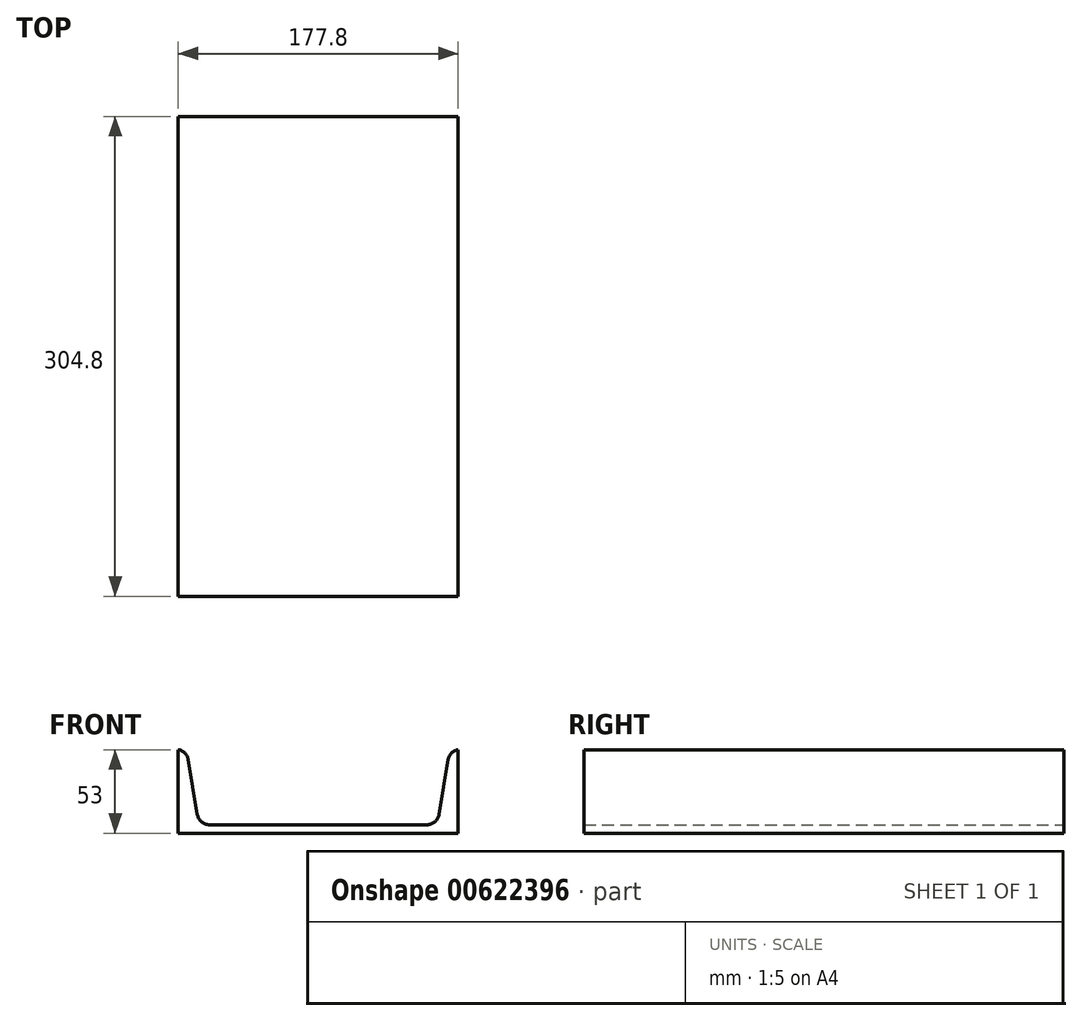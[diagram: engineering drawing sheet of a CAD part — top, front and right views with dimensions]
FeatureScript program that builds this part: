
annotation { "Feature Type Name" : "Feature", "Feature Type Description" : "" }
export const myFeature = defineFeature(function(context is Context, id is Id, definition is map)
    precondition{}
    {
        {
            var Q0;
            Q0=qCreatedBy(makeId("Front.planeOp"),FACE);
            var sketch = newSketch(context, id + "F0", { "sketchPlane" : qUnion([Q0])});
            skLineSegment(sketch, "E0", {"start": v(0, 0) * mm, "end": v(177.8, 0) * mm});
            skLineSegment(sketch, "E1", {"start": v(177.8, 0) * mm, "end": v(177.8, 53.09) * mm});
            skLineSegment(sketch, "E2", {"start": v(178.93, 53.09) * mm, "end": v(177.8, 53.09) * mm});
            skLineSegment(sketch, "E3", {"start": v(157.91, 5.33) * mm, "end": v(19.89, 5.33) * mm});
            skLineSegment(sketch, "E4", {"start": v(0, 53.09) * mm, "end": v(-1.13, 53.09) * mm});
            skLineSegment(sketch, "E5", {"start": v(0, 53.09) * mm, "end": v(0, 0) * mm});
            skLineSegment(sketch, "E6", {"start": v(171.41, 46.7) * mm, "end": v(165.68, 11.93) * mm});
            skPoint(sketch, "E7.visualSharp", {"position": v(164.6, 5.33) * mm});
            skArc(sketch, "E7.filletArc", {"start": v(157.91, 5.33) * mm, "mid": v(163, 7.2) * mm, "end": v(165.68, 11.93) * mm});
            skLineSegment(sketch, "E8", {"start": v(12.12, 11.93) * mm, "end": v(6.39, 46.7) * mm});
            skPoint(sketch, "E9.visualSharp", {"position": v(13.2, 5.33) * mm});
            skArc(sketch, "E9.filletArc", {"start": v(12.12, 11.93) * mm, "mid": v(14.8, 7.2) * mm, "end": v(19.89, 5.33) * mm});
            skPoint(sketch, "E10.visualSharp", {"position": v(5.33, 53.09) * mm});
            skArc(sketch, "E10.filletArc", {"start": v(6.39, 46.7) * mm, "mid": v(3.8, 51.28) * mm, "end": v(-1.13, 53.09) * mm});
            skPoint(sketch, "E11.visualSharp", {"position": v(172.47, 53.09) * mm});
            skArc(sketch, "E11.filletArc", {"start": v(178.93, 53.09) * mm, "mid": v(174, 51.28) * mm, "end": v(171.41, 46.7) * mm});
            skSolve(sketch);
        }
        {
            var Q0;
            {var subQ1=sQuery(id+"F0.wireOp",EDGE,"E0");Q0=makeQuery(id+"F0.imprint","IMPRINT",FACE,{"disambiguationData":[TD([[makeQuery(id+"F0.imprint","IMPRINT",EDGE,{"derivedFrom":subQ1}),1.0]])]});}
            extrude(context, id + "F1", {"entities" : qUnion([Q0]), "depth" : 304.8 * mm, "offsetDistance" : 30.48 * mm});
        }
    });
